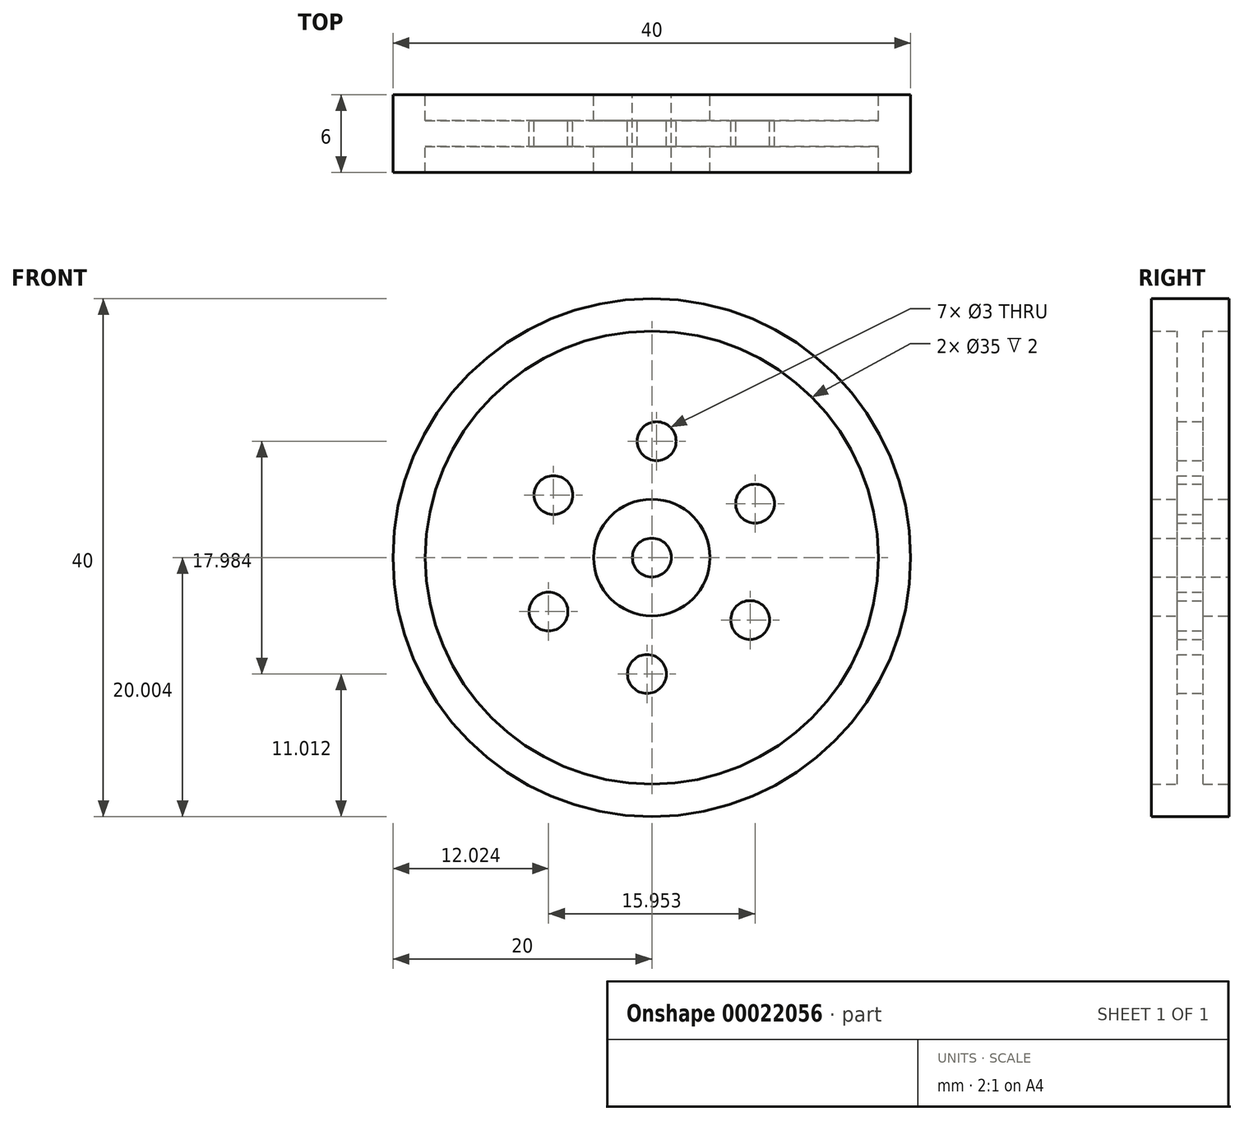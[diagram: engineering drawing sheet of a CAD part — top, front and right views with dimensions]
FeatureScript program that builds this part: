
annotation { "Feature Type Name" : "Feature", "Feature Type Description" : "" }
export const myFeature = defineFeature(function(context is Context, id is Id, definition is map)
    precondition{}
    {
        {
            var Q0;
            Q0=qCreatedBy(makeId("Front.planeOp"),FACE);
            var sketch = newSketch(context, id + "F0", { "sketchPlane" : qUnion([Q0])});
            skCircle(sketch, "E0", {"center": v(-73.88, 14.3) * mm, "radius": 20 * mm});
            skCircle(sketch, "E1", {"center": v(-73.88, 14.3) * mm, "radius": 4.5 * mm});
            skCircle(sketch, "E2", {"center": v(-73.88, 14.3) * mm, "radius": 1.5 * mm});
            skCircle(sketch, "E3", {"center": v(-73.88, 14.3) * mm, "radius": 17.5 * mm});
            skCircle(sketch, "E4", {"center": v(-73.5, 23.3) * mm, "radius": 1.5 * mm});
            skCircle(sketch, "E5.1.0", {"center": v(12.33, -72.18) * mm, "radius": 1.5 * mm});
            skCircle(sketch, "E5.2.0", {"center": v(52.1, 49.9) * mm, "radius": 1.5 * mm});
            skCircle(sketch, "E6.1.0", {"center": v(-81.48, 19.13) * mm, "radius": 1.5 * mm});
            skCircle(sketch, "E6.2.0", {"center": v(-81.86, 10.14) * mm, "radius": 1.5 * mm});
            skCircle(sketch, "E6.3.0", {"center": v(-74.26, 5.31) * mm, "radius": 1.5 * mm});
            skCircle(sketch, "E6.4.0", {"center": v(-66.28, 9.48) * mm, "radius": 1.5 * mm});
            skCircle(sketch, "E6.5.0", {"center": v(-65.9, 18.47) * mm, "radius": 1.5 * mm});
            skSolve(sketch);
        }
        {
            var Q0;
            Q0=makeQuery(id+"F0.imprint","IMPRINT",FACE,{"disambiguationData":[TD([[makeQuery(id+"F0.imprint","IMPRINT",EDGE,{"derivedFrom":sQuery(id+"F0.wireOp",EDGE,"E0")}),1.0]])]});
            extrude(context, id + "F1", {"entities" : qUnion([Q0]), "endBound" : BoundingType.SYMMETRIC, "depth" : 6 * mm});
        }
        {
            var Q0;
            Q0=makeQuery(id+"F0.imprint","IMPRINT",FACE,{"disambiguationData":[TD([[makeQuery(id+"F0.imprint","IMPRINT",EDGE,{"derivedFrom":sQuery(id+"F0.wireOp",EDGE,"E1")}),-1.0]])]});
            extrude(context, id + "F2", {"entities" : qUnion([Q0]), "operationType" : NewBodyOperationType.ADD, "endBound" : BoundingType.SYMMETRIC, "depth" : 2 * mm});
        }
        {
            var Q0;
            Q0=makeQuery(id+"F0.imprint","IMPRINT",FACE,{"disambiguationData":[TD([[makeQuery(id+"F0.imprint","IMPRINT",EDGE,{"derivedFrom":sQuery(id+"F0.wireOp",EDGE,"E1")}),1.0]])]});
            extrude(context, id + "F3", {"entities" : qUnion([Q0]), "operationType" : NewBodyOperationType.ADD, "endBound" : BoundingType.SYMMETRIC, "depth" : 6 * mm});
        }
    });
